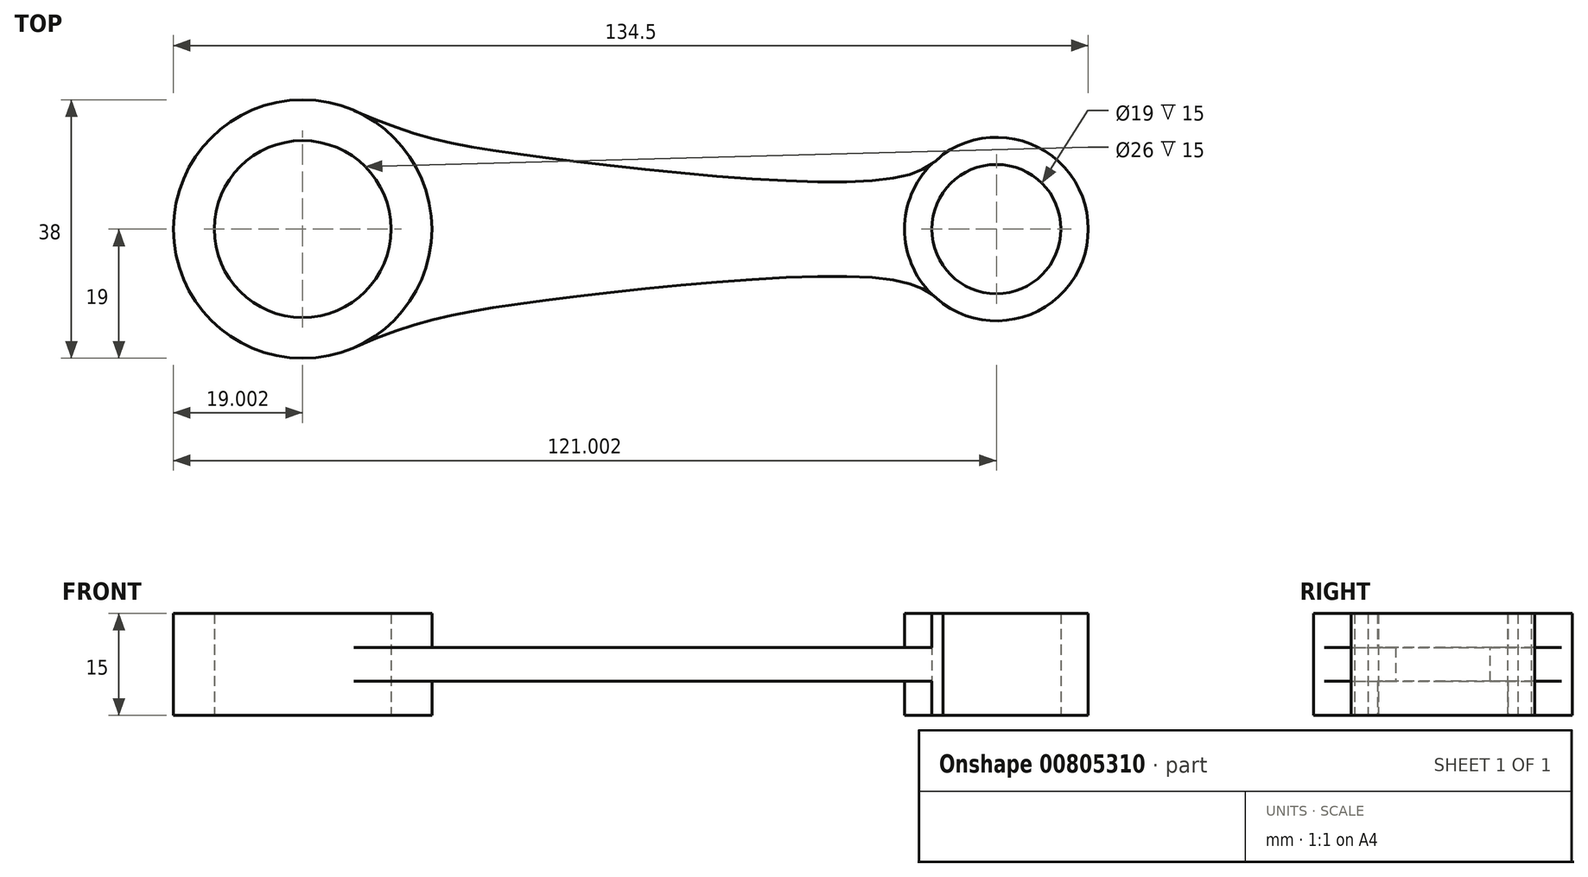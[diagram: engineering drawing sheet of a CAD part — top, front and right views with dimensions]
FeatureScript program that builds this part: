
annotation { "Feature Type Name" : "Feature", "Feature Type Description" : "" }
export const myFeature = defineFeature(function(context is Context, id is Id, definition is map)
    precondition{}
    {
        {
            var Q0;
            Q0=qCreatedBy(makeId("Top.planeOp"),FACE);
            var sketch = newSketch(context, id + "F0", { "sketchPlane" : qUnion([Q0])});
            skCircle(sketch, "E0", {"center": v(-48.59, 0) * mm, "radius": 19 * mm});
            skCircle(sketch, "E1", {"center": v(53.41, 0) * mm, "radius": 13.5 * mm});
            skLineSegment(sketch, "E2", {"start": v(-34.73, 13) * mm, "end": v(-34.73, -13) * mm, "construction": true});
            skLineSegment(sketch, "E3", {"start": v(45.59, 11) * mm, "end": v(45.59, -11) * mm, "construction": true});
            skPoint(sketch, "E4", {"position": v(38.41, 0) * mm});
            skLineSegment(sketch, "E5", {"start": v(38.41, 7.5) * mm, "end": v(38.41, -7.5) * mm, "construction": true});
            skPoint(sketch, "E6", {"position": v(-16.59, 0) * mm});
            skLineSegment(sketch, "E7", {"start": v(-16.59, 11) * mm, "end": v(-16.59, -11) * mm, "construction": true});
            skFitSpline(sketch, "E8", {"points": [v(-41.02, 17.43) * mm, v(-16.59, 11) * mm, v(38.41, 7.5) * mm, v(45.59, 11) * mm], "startDerivative": vector(83.77, -36.36) * mm, "endDerivative": vector(23.6, 21.86) * mm});
            skFitSpline(sketch, "E9.MirrorCS", {"points": [v(-41.02, -17.43) * mm, v(-16.59, -11) * mm, v(38.41, -7.5) * mm, v(45.59, -11) * mm], "startDerivative": vector(83.77, 36.36) * mm, "endDerivative": vector(23.6, -21.86) * mm});
            skCircle(sketch, "E10", {"center": v(-48.59, 0) * mm, "radius": 13 * mm});
            skCircle(sketch, "E11", {"center": v(53.41, 0) * mm, "radius": 9.5 * mm});
            skPoint(sketch, "E12", {"position": v(29.06, 0) * mm});
            skPoint(sketch, "E13", {"position": v(-25.94, 0) * mm});
            skSolve(sketch);
        }
        {
            var Q0;
            Q0=makeQuery(id+"F0.imprint","IMPRINT",FACE,{"disambiguationData":[TD([[makeQuery(id+"F0.imprint","IMPRINT",EDGE,{"derivedFrom":sQuery(id+"F0.wireOp",EDGE,"E11")}),-1.0]])]});
            extrude(context, id + "F1", {"entities" : qUnion([Q0]), "depth" : 7.5 * mm, "offsetDistance" : 25 * mm, "hasSecondDirection" : true, "secondDirectionOppositeDirection" : true, "secondDirectionDepth" : 7.5 * mm});
        }
        {
            var Q0;
            {var subQ0=sQuery(id+"F0.wireOp",EDGE,"E8");var subQ1=sQuery(id+"F0.wireOp",EDGE,"E0");var subQ2=makeQuery(id+"F0.imprint","INTERSECT",VERTEX,{"derivedFrom":[subQ1,subQ0]});Q0=makeQuery(id+"F0.imprint","IMPRINT",FACE,{"disambiguationData":[TD([[makeQuery(id+"F0.imprint","IMPRINT",EDGE,{"disambiguationData":[TD([[subQ2,1.0]])],"derivedFrom":subQ1}),-1.0]])]});}
            extrude(context, id + "F2", {"entities" : qUnion([Q0]), "operationType" : NewBodyOperationType.ADD, "depth" : 2.5 * mm, "offsetDistance" : 25 * mm, "hasSecondDirection" : true, "secondDirectionOppositeDirection" : true, "secondDirectionDepth" : 2.5 * mm});
        }
        {
            var Q0;
            Q0=makeQuery(id+"F0.imprint","IMPRINT",FACE,{"disambiguationData":[TD([[makeQuery(id+"F0.imprint","IMPRINT",EDGE,{"derivedFrom":sQuery(id+"F0.wireOp",EDGE,"E10")}),-1.0]])]});
            extrude(context, id + "F3", {"entities" : qUnion([Q0]), "operationType" : NewBodyOperationType.ADD, "depth" : 7.5 * mm, "offsetDistance" : 25 * mm, "hasSecondDirection" : true, "secondDirectionOppositeDirection" : true, "secondDirectionDepth" : 7.5 * mm});
        }
    });
